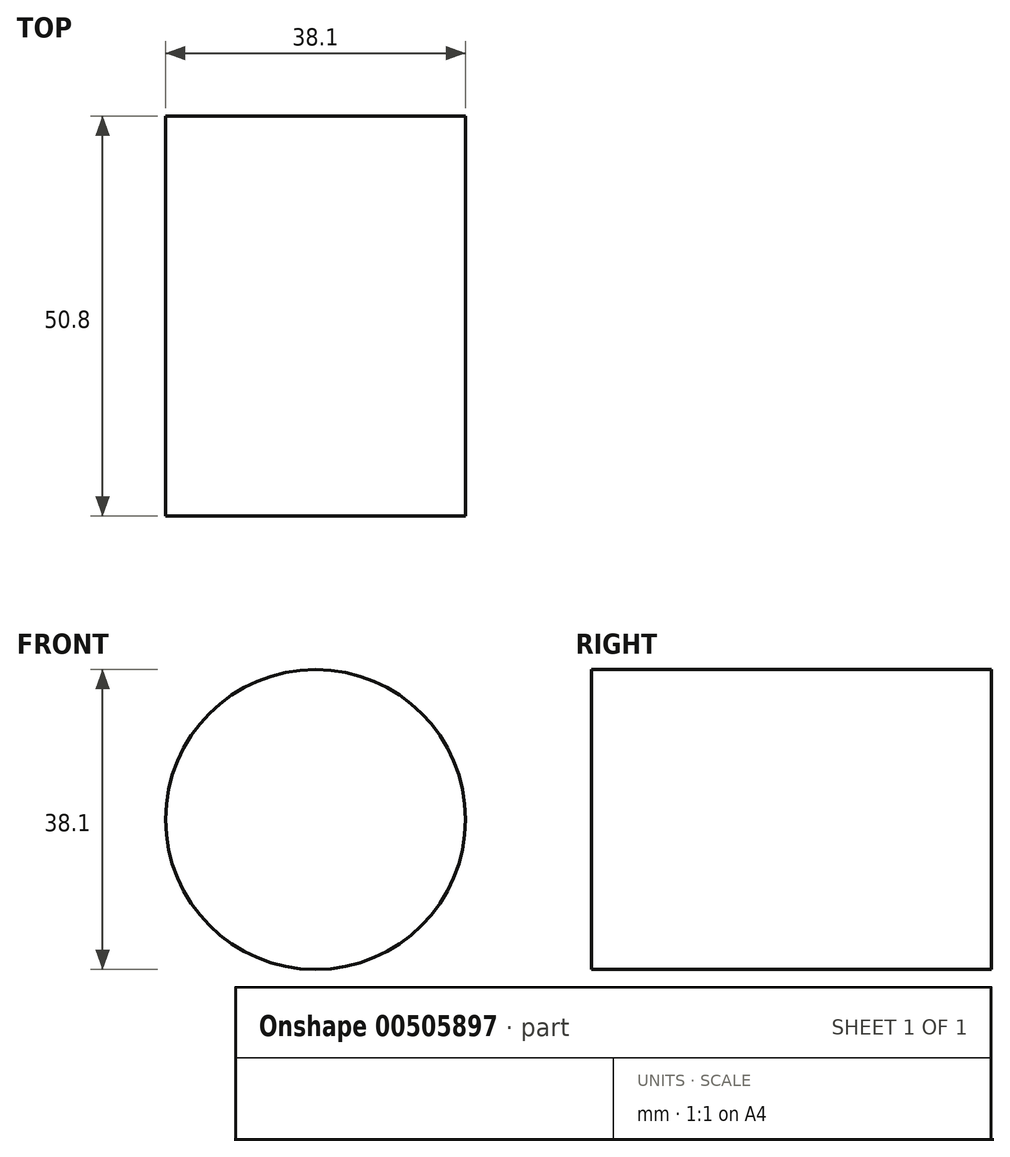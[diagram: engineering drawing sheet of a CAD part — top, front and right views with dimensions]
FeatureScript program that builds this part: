
annotation { "Feature Type Name" : "Feature", "Feature Type Description" : "" }
export const myFeature = defineFeature(function(context is Context, id is Id, definition is map)
    precondition{}
    {
        {
            var Q0;
            Q0=qCreatedBy(makeId("Front.planeOp"),FACE);
            var sketch = newSketch(context, id + "F0", { "sketchPlane" : qUnion([Q0])});
            skCircle(sketch, "E0", {"center": v(0, 0) * mm, "radius": 19.05 * mm});
            skSolve(sketch);
        }
        {
            var Q0;
            Q0 = qSketchRegion(id + "F0", true);
            extrude(context, id + "F1", {"entities" : qUnion([Q0]), "depth" : 50.8 * mm});
        }
    });
